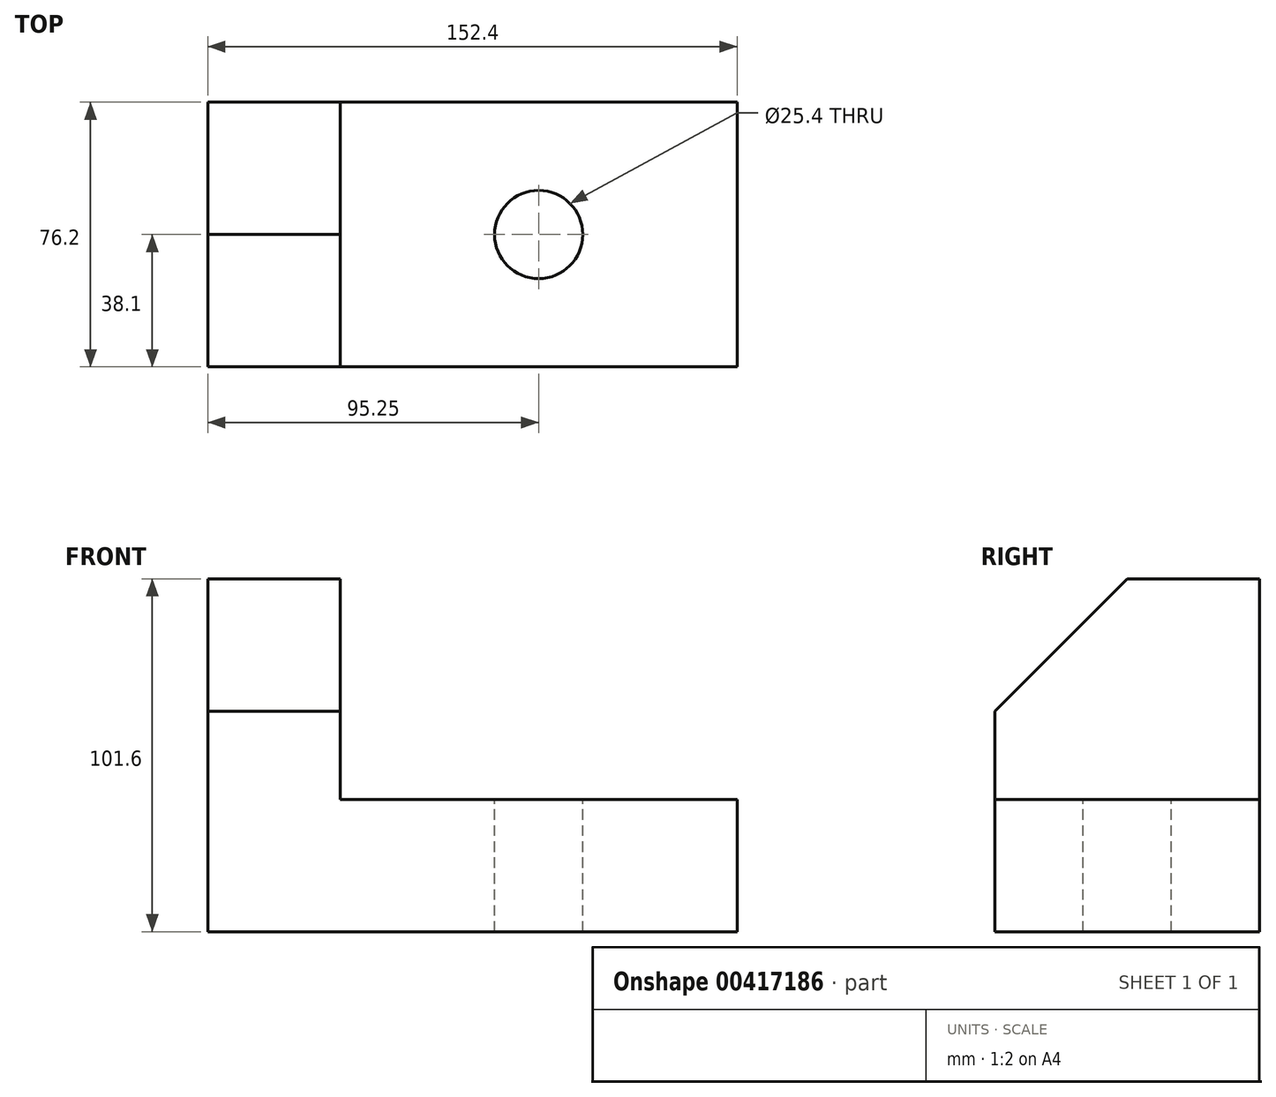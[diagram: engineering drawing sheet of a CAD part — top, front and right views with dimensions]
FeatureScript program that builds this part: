
annotation { "Feature Type Name" : "Feature", "Feature Type Description" : "" }
export const myFeature = defineFeature(function(context is Context, id is Id, definition is map)
    precondition{}
    {
        {
            var Q0;
            Q0=qCreatedBy(makeId("Front.planeOp"),FACE);
            var sketch = newSketch(context, id + "F0", { "sketchPlane" : qUnion([Q0])});
            skLineSegment(sketch, "E0", {"start": v(0, 0) * mm, "end": v(152.4, 0) * mm});
            skLineSegment(sketch, "E1", {"start": v(152.4, 0) * mm, "end": v(152.4, 38.1) * mm});
            skLineSegment(sketch, "E2", {"start": v(152.4, 38.1) * mm, "end": v(38.1, 38.1) * mm});
            skLineSegment(sketch, "E3", {"start": v(38.1, 38.1) * mm, "end": v(38.1, 101.6) * mm});
            skLineSegment(sketch, "E4", {"start": v(38.1, 101.6) * mm, "end": v(0, 101.6) * mm});
            skLineSegment(sketch, "E5", {"start": v(0, 0) * mm, "end": v(0, 101.6) * mm});
            skSolve(sketch);
        }
        {
            var Q0;
            Q0=makeQuery(id+"F0.imprint","IMPRINT",FACE,{"disambiguationData":[TD([[makeQuery(id+"F0.imprint","IMPRINT",EDGE,{"derivedFrom":sQuery(id+"F0.wireOp",EDGE,"E0")}),1.0]])]});
            extrude(context, id + "F1", {"entities" : qUnion([Q0]), "depth" : 76.2 * mm});
        }
        {
            var Q0;
            Q0=makeQuery(id+"F1.opExtrude","SWEPT_FACE",FACE,{"disambiguationData":[OSD([sQuery(id+"F0.wireOp",EDGE,"E3")])]});
            var sketch = newSketch(context, id + "F2", { "sketchPlane" : qUnion([Q0])});
            skLineSegment(sketch, "E6", {"start": v(-38.1, 101.6) * mm, "end": v(-76.2, 63.5) * mm});
            skLineSegment(sketch, "E7", {"start": v(-76.2, 101.6) * mm, "end": v(-76.2, 63.5) * mm});
            skLineSegment(sketch, "E8", {"start": v(-76.2, 101.6) * mm, "end": v(-38.1, 101.6) * mm});
            skSolve(sketch);
        }
        {
            var Q0;
            Q0=makeQuery(id+"F2.imprint","IMPRINT",FACE,{"disambiguationData":[TD([[makeQuery(id+"F2.imprint","IMPRINT",EDGE,{"derivedFrom":sQuery(id+"F2.wireOp",EDGE,"E6")}),-1.0]])]});
            extrude(context, id + "F3", {"entities" : qUnion([Q0]), "operationType" : NewBodyOperationType.REMOVE, "endBound" : BoundingType.THROUGH_ALL, "oppositeDirection" : true, "depth" : 25.4 * mm});
        }
        {
            var Q0;
            Q0=makeQuery(id+"F1.opExtrude","SWEPT_FACE",FACE,{"disambiguationData":[OSD([sQuery(id+"F0.wireOp",EDGE,"E2")])]});
            var sketch = newSketch(context, id + "F4", { "sketchPlane" : qUnion([Q0])});
            skCircle(sketch, "E9", {"center": v(95.25, -38.1) * mm, "radius": 12.7 * mm});
            skSolve(sketch);
        }
        {
            var Q0;
            Q0=makeQuery(id+"F4.imprint","IMPRINT",FACE,{"disambiguationData":[TD([[makeQuery(id+"F4.imprint","IMPRINT",EDGE,{"derivedFrom":sQuery(id+"F4.wireOp",EDGE,"E9")}),1.0]])]});
            extrude(context, id + "F5", {"entities" : qUnion([Q0]), "operationType" : NewBodyOperationType.REMOVE, "endBound" : BoundingType.THROUGH_ALL, "oppositeDirection" : true, "depth" : 25.4 * mm});
        }
    });
